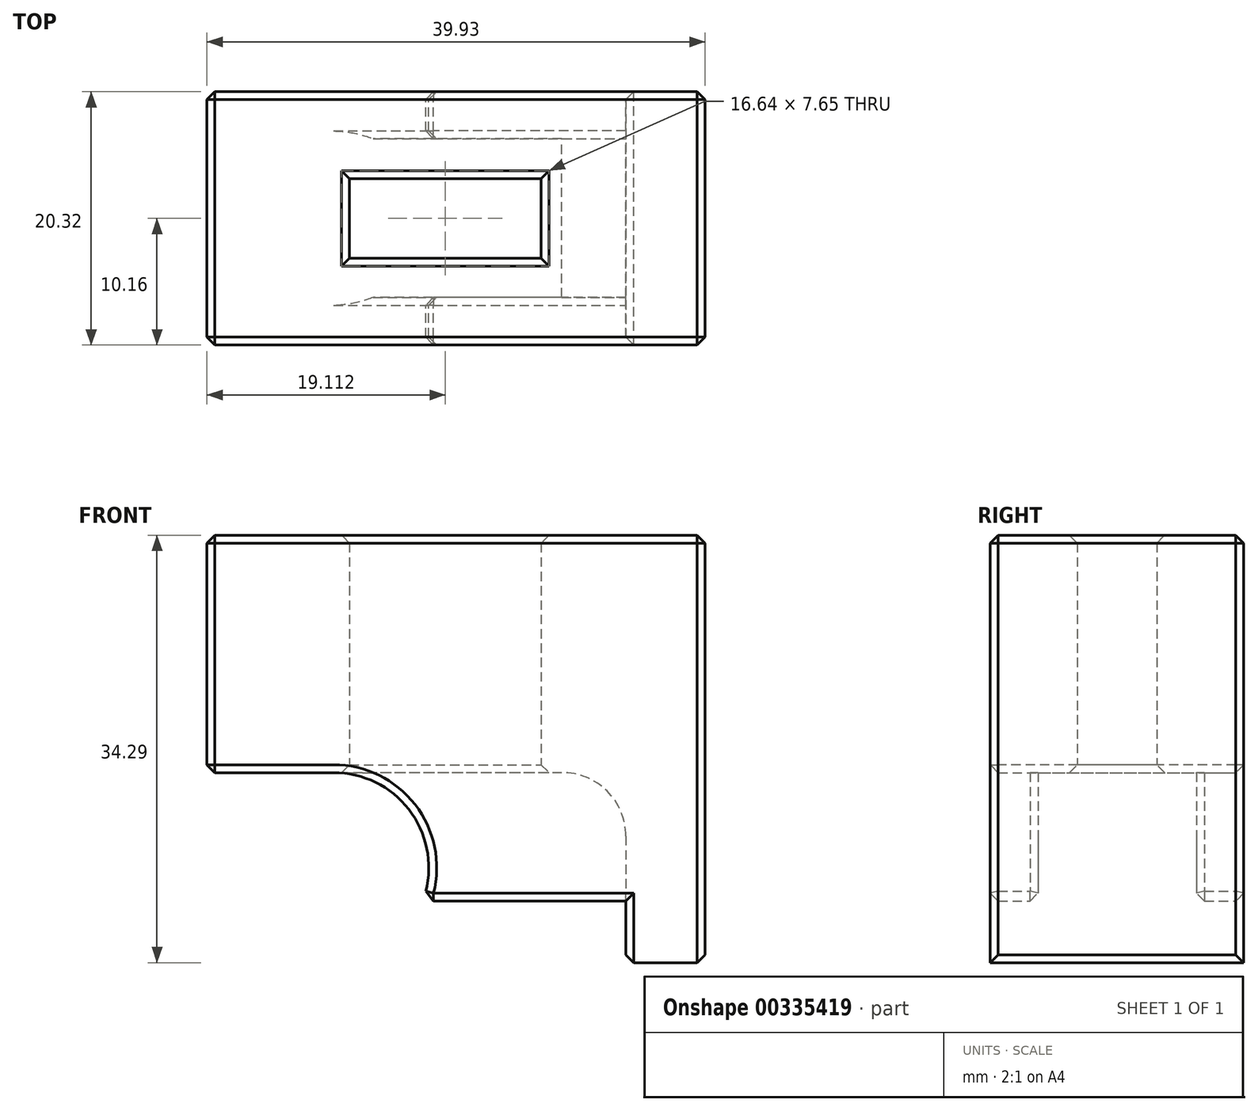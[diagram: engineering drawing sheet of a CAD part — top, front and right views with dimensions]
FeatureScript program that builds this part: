
annotation { "Feature Type Name" : "Feature", "Feature Type Description" : "" }
export const myFeature = defineFeature(function(context is Context, id is Id, definition is map)
    precondition{}
    {
        {
            var Q0;
            Q0=qCreatedBy(makeId("Top.planeOp"),FACE);
            var sketch = newSketch(context, id + "F0", { "sketchPlane" : qUnion([Q0])});
            skLineSegment(sketch, "E0.bottom", {"start": v(4, 3.19) * mm, "end": v(-11.37, 3.19) * mm});
            skLineSegment(sketch, "E0.top", {"start": v(4, -3.19) * mm, "end": v(-11.37, -3.19) * mm});
            skLineSegment(sketch, "E0.left", {"start": v(4, 3.19) * mm, "end": v(4, -3.19) * mm});
            skLineSegment(sketch, "E0.right", {"start": v(-11.37, 3.19) * mm, "end": v(-11.37, -3.19) * mm});
            skPoint(sketch, "E0.middle", {"position": v(-3.69, 0) * mm});
            skLineSegment(sketch, "E1.bottom", {"start": v(10.78, -12.7) * mm, "end": v(-12.64, -12.7) * mm});
            skLineSegment(sketch, "E1.top", {"start": v(10.78, 12.7) * mm, "end": v(-12.64, 12.7) * mm});
            skLineSegment(sketch, "E1.left", {"start": v(10.78, -12.7) * mm, "end": v(10.78, 12.7) * mm});
            skLineSegment(sketch, "E1.right", {"start": v(-12.64, -12.7) * mm, "end": v(-12.64, 12.7) * mm});
            skPoint(sketch, "E1.middle", {"position": v(-0.93, 0) * mm});
            skSolve(sketch);
        }
        {
            var Q0;
            Q0 = qSketchRegion(id + "F0", true);
            extrude(context, id + "F1", {"entities" : qUnion([Q0]), "depth" : 34.3 * mm});
        }
        {
            var Q0;
            Q0=makeQuery(id+"F1.opExtrude","SWEPT_FACE",FACE,{"disambiguationData":[OSD([sQuery(id+"F0.wireOp",EDGE,"E1.top")])]});
            var sketch = newSketch(context, id + "F2", { "sketchPlane" : qUnion([Q0])});
            skCircle(sketch, "E2", {"center": v(12.64, 7.62) * mm, "radius": 7.62 * mm});
            skSolve(sketch);
        }
        {
            var Q0;
            Q0 = qSketchRegion(id + "F2", true);
            extrude(context, id + "F3", {"entities" : qUnion([Q0]), "operationType" : NewBodyOperationType.REMOVE, "oppositeDirection" : true, "depth" : 25.4 * mm});
        }
        {
            var Q0;
            Q0=makeQuery(id+"F1.opExtrude","SWEPT_FACE",FACE,{"disambiguationData":[OSD([sQuery(id+"F0.wireOp",EDGE,"E1.right")])]});
            var sketch = newSketch(context, id + "F4", { "sketchPlane" : qUnion([Q0])});
            skLineSegment(sketch, "E3.bottom", {"start": v(-6.38, 15.24) * mm, "end": v(6.34, 15.24) * mm});
            skLineSegment(sketch, "E3.top", {"start": v(-6.38, 0) * mm, "end": v(6.34, 0) * mm});
            skLineSegment(sketch, "E3.left", {"start": v(-6.38, 15.24) * mm, "end": v(-6.38, 0) * mm});
            skLineSegment(sketch, "E3.right", {"start": v(6.34, 15.24) * mm, "end": v(6.34, 0) * mm});
            skSolve(sketch);
        }
        {
            var Q0;
            Q0 = qSketchRegion(id + "F4", true);
            extrude(context, id + "F5", {"entities" : qUnion([Q0]), "operationType" : NewBodyOperationType.REMOVE, "oppositeDirection" : true, "depth" : 18.29 * mm});
        }
        {
            var Q0;
            Q0=makeQuery(id+"F1.opExtrude","SWEPT_FACE",FACE,{"disambiguationData":[OSD([sQuery(id+"F0.wireOp",EDGE,"E1.left")])]});
            var sketch = newSketch(context, id + "F6", { "sketchPlane" : qUnion([Q0])});
            skLineSegment(sketch, "E4.bottom", {"start": v(-12.7, 34.3) * mm, "end": v(12.7, 34.3) * mm});
            skLineSegment(sketch, "E4.top", {"start": v(-12.7, 0) * mm, "end": v(12.7, 0) * mm});
            skLineSegment(sketch, "E4.left", {"start": v(-12.7, 34.3) * mm, "end": v(-12.7, 0) * mm});
            skLineSegment(sketch, "E4.right", {"start": v(12.7, 34.3) * mm, "end": v(12.7, 0) * mm});
            skSolve(sketch);
        }
        {
            var Q0;
            Q0 = qSketchRegion(id + "F6", true);
            extrude(context, id + "F7", {"entities" : qUnion([Q0]), "operationType" : NewBodyOperationType.ADD, "depth" : 6.35 * mm});
        }
        {
            var Q0;
            Q0=makeQuery(id+"F7.boolean.opBoolean","MERGE",FACE,{"derivedFrom":[makeQuery(id+"F1.opExtrude","SWEPT_FACE",FACE,{"disambiguationData":[OSD([sQuery(id+"F0.wireOp",EDGE,"E1.top")])]}),makeQuery(id+"F7.opExtrude","SWEPT_FACE",FACE,{"disambiguationData":[OSD([sQuery(id+"F6.wireOp",EDGE,"E4.right")])]})]});
            cPlane(context, id + "F8", {"entities" : qUnion([Q0]), "cplaneType" : CPlaneType.OFFSET, "offset" : 6.32 * mm, "oppositeDirection" : true, "width" : 152.4 * mm, "height" : 152.4 * mm});
        }
        {
            var Q0;
            Q0=qCreatedBy(id+"F8.planeOp",FACE);
            var sketch = newSketch(context, id + "F9", { "sketchPlane" : qUnion([Q0])});
            skCircle(sketch, "E5", {"center": v(-5.7, 10.16) * mm, "radius": 5.08 * mm});
            skLineSegment(sketch, "E6", {"start": v(-10.78, 10.16) * mm, "end": v(-10.78, 0) * mm});
            skLineSegment(sketch, "E7", {"start": v(-10.78, 0) * mm, "end": v(-0.62, 0) * mm});
            skLineSegment(sketch, "E8", {"start": v(-0.62, 0) * mm, "end": v(-0.62, 10.16) * mm});
            skSolve(sketch);
        }
        {
            var Q0;
            Q0 = qSketchRegion(id + "F9", true);
            extrude(context, id + "F10", {"entities" : qUnion([Q0]), "operationType" : NewBodyOperationType.REMOVE, "oppositeDirection" : true, "depth" : 12.71 * mm});
        }
        {
            var Q0;
            Q0=makeQuery(id+"F7.boolean.opBoolean","MERGE",FACE,{"derivedFrom":[makeQuery(id+"F1.opExtrude","SWEPT_FACE",FACE,{"disambiguationData":[OSD([sQuery(id+"F0.wireOp",EDGE,"E1.top")])]}),makeQuery(id+"F7.opExtrude","SWEPT_FACE",FACE,{"disambiguationData":[OSD([sQuery(id+"F6.wireOp",EDGE,"E4.right")])]})]});
            var sketch = newSketch(context, id + "F11", { "sketchPlane" : qUnion([Q0])});
            skLineSegment(sketch, "E9.bottom", {"start": v(12.64, 4.93) * mm, "end": v(-10.78, 4.93) * mm});
            skLineSegment(sketch, "E9.top", {"start": v(12.64, -3.43) * mm, "end": v(-10.78, -3.43) * mm});
            skLineSegment(sketch, "E9.left", {"start": v(12.64, 4.93) * mm, "end": v(12.64, -3.43) * mm});
            skLineSegment(sketch, "E9.right", {"start": v(-10.78, 4.93) * mm, "end": v(-10.78, -3.43) * mm});
            skSolve(sketch);
        }
        {
            var Q0;
            Q0 = qSketchRegion(id + "F11", true);
            extrude(context, id + "F12", {"entities" : qUnion([Q0]), "operationType" : NewBodyOperationType.REMOVE, "oppositeDirection" : true, "depth" : 25.4 * mm});
        }
        {
            var Q0;
            Q0=makeQuery(id+"F1.opExtrude","SWEPT_FACE",FACE,{"disambiguationData":[OSD([sQuery(id+"F0.wireOp",EDGE,"E1.right")])]});
            var sketch = newSketch(context, id + "F13", { "sketchPlane" : qUnion([Q0])});
            skLineSegment(sketch, "E10.bottom", {"start": v(-12.7, 34.3) * mm, "end": v(-10.16, 34.3) * mm});
            skLineSegment(sketch, "E10.top", {"start": v(-12.7, 0) * mm, "end": v(-10.16, 0) * mm});
            skLineSegment(sketch, "E10.left", {"start": v(-12.7, 34.3) * mm, "end": v(-12.7, 0) * mm});
            skLineSegment(sketch, "E10.right", {"start": v(-10.16, 34.3) * mm, "end": v(-10.16, 0) * mm});
            skLineSegment(sketch, "E11.bottom", {"start": v(12.7, 34.3) * mm, "end": v(10.16, 34.3) * mm});
            skLineSegment(sketch, "E11.top", {"start": v(12.7, 0) * mm, "end": v(10.16, 0) * mm});
            skLineSegment(sketch, "E11.left", {"start": v(12.7, 34.3) * mm, "end": v(12.7, 0) * mm});
            skLineSegment(sketch, "E11.right", {"start": v(10.16, 34.3) * mm, "end": v(10.16, 0) * mm});
            skSolve(sketch);
        }
        {
            var Q0;
            Q0 = qSketchRegion(id + "F13", true);
            extrude(context, id + "F14", {"entities" : qUnion([Q0]), "operationType" : NewBodyOperationType.REMOVE, "endBound" : BoundingType.THROUGH_ALL, "oppositeDirection" : true, "depth" : 25.4 * mm});
        }
        {
            var Q0;
            Q0=makeQuery(id+"F1.opExtrude","SWEPT_FACE",FACE,{"disambiguationData":[OSD([sQuery(id+"F0.wireOp",EDGE,"E1.right")])]});
            var sketch = newSketch(context, id + "F15", { "sketchPlane" : qUnion([Q0])});
            skLineSegment(sketch, "E12.bottom", {"start": v(-10.16, 15.24) * mm, "end": v(10.16, 15.24) * mm});
            skLineSegment(sketch, "E12.top", {"start": v(-10.16, 34.3) * mm, "end": v(10.16, 34.3) * mm});
            skLineSegment(sketch, "E12.left", {"start": v(-10.16, 15.24) * mm, "end": v(-10.16, 34.3) * mm});
            skLineSegment(sketch, "E12.right", {"start": v(10.16, 15.24) * mm, "end": v(10.16, 34.3) * mm});
            skSolve(sketch);
        }
        {
            var Q0;
            Q0 = qSketchRegion(id + "F15", true);
            extrude(context, id + "F16", {"entities" : qUnion([Q0]), "operationType" : NewBodyOperationType.ADD, "depth" : 10.16 * mm});
        }
        {
            var Q0;
            Q0=makeQuery(id+"F1.opExtrude","CAP_EDGE",EDGE,{"disambiguationData":[OSD([sQuery(id+"F0.wireOp",EDGE,"E0.top")])],"isStart":false});
            var Q1;
            Q1=makeQuery(id+"F1.opExtrude","CAP_EDGE",EDGE,{"disambiguationData":[OSD([sQuery(id+"F0.wireOp",EDGE,"E0.left")])],"isStart":false});
            var Q2;
            Q2=makeQuery(id+"F1.opExtrude","CAP_EDGE",EDGE,{"disambiguationData":[OSD([sQuery(id+"F0.wireOp",EDGE,"E0.bottom")])],"isStart":false});
            var Q3;
            Q3=makeQuery(id+"F1.opExtrude","CAP_EDGE",EDGE,{"disambiguationData":[OSD([sQuery(id+"F0.wireOp",EDGE,"E0.right")])],"isStart":false});
            var Q4;
            Q4=makeQuery(id+"F16.boolean.opBoolean","MERGE",EDGE,{"derivedFrom":[makeQuery(id+"F14.boolean.opBoolean","COPY",EDGE,{"derivedFrom":makeQuery(id+"F14.opExtrude","SWEPT_EDGE",EDGE,{"disambiguationData":[OSD([sQuery(id+"F0.wireOp",EDGE,"E1.right"),sQuery(id+"F13.wireOp",EDGE,"E10.bottom"),sQuery(id+"F13.wireOp",EDGE,"E10.right")])]})}),makeQuery(id+"F16.opExtrude","SWEPT_EDGE",EDGE,{"disambiguationData":[OSD([sQuery(id+"F15.wireOp",EDGE,"E12.top"),sQuery(id+"F15.wireOp",EDGE,"E12.left")])]})]});
            var Q5;
            Q5=makeQuery(id+"F7.opExtrude","CAP_EDGE",EDGE,{"disambiguationData":[OSD([sQuery(id+"F6.wireOp",EDGE,"E4.bottom")])],"isStart":false});
            var Q6;
            Q6=makeQuery(id+"F16.boolean.opBoolean","MERGE",FACE,{"derivedFrom":[makeQuery(id+"F7.boolean.opBoolean","MERGE",FACE,{"derivedFrom":[makeQuery(id+"F1.opExtrude","CAP_FACE",FACE,{"disambiguationData":[OSD([sQuery(id+"F0.wireOp",EDGE,"E0.bottom"),sQuery(id+"F0.wireOp",EDGE,"E0.top"),sQuery(id+"F0.wireOp",EDGE,"E0.left"),sQuery(id+"F0.wireOp",EDGE,"E0.right"),sQuery(id+"F0.wireOp",EDGE,"E1.bottom"),sQuery(id+"F0.wireOp",EDGE,"E1.top"),sQuery(id+"F0.wireOp",EDGE,"E1.left"),sQuery(id+"F0.wireOp",EDGE,"E1.right")])],"isStart":false}),makeQuery(id+"F7.opExtrude","SWEPT_FACE",FACE,{"disambiguationData":[OSD([sQuery(id+"F6.wireOp",EDGE,"E4.bottom")])]})]}),makeQuery(id+"F16.opExtrude","SWEPT_FACE",FACE,{"disambiguationData":[OSD([sQuery(id+"F15.wireOp",EDGE,"E12.top")])]})]});
            var Q7;
            Q7=makeQuery(id+"F16.opExtrude","CAP_EDGE",EDGE,{"disambiguationData":[OSD([sQuery(id+"F15.wireOp",EDGE,"E12.left")])],"isStart":false});
            var Q8;
            Q8=makeQuery(id+"F14.boolean.opBoolean","INTERSECT",EDGE,{"derivedFrom":[makeQuery(id+"F12.boolean.opBoolean","COPY",FACE,{"disambiguationData":[TD([makeQuery(id+"F1.opExtrude","SWEPT_FACE",FACE,{"disambiguationData":[OSD([sQuery(id+"F0.wireOp",EDGE,"E1.top")])]})])],"derivedFrom":makeQuery(id+"F12.opExtrude","SWEPT_FACE",FACE,{"disambiguationData":[OSD([sQuery(id+"F11.wireOp",EDGE,"E9.bottom")])]})}),makeQuery(id+"F14.opExtrude","SWEPT_FACE",FACE,{"disambiguationData":[OSD([sQuery(id+"F13.wireOp",EDGE,"E10.right")])]})]});
            var Q9;
            Q9=makeQuery(id+"F14.boolean.opBoolean","INTERSECT",EDGE,{"derivedFrom":[makeQuery(id+"F12.boolean.opBoolean","MERGE",FACE,{"derivedFrom":[makeQuery(id+"F10.boolean.opBoolean","COPY",FACE,{"derivedFrom":makeQuery(id+"F10.opExtrude","SWEPT_FACE",FACE,{"disambiguationData":[OSD([sQuery(id+"F9.wireOp",EDGE,"E6")])]})}),makeQuery(id+"F12.opExtrude","SWEPT_FACE",FACE,{"disambiguationData":[OSD([sQuery(id+"F11.wireOp",EDGE,"E9.right")])]})]}),makeQuery(id+"F14.opExtrude","SWEPT_FACE",FACE,{"disambiguationData":[OSD([sQuery(id+"F13.wireOp",EDGE,"E10.right")])]})]});
            var Q10;
            Q10=makeQuery(id+"F14.boolean.opBoolean","INTERSECT",EDGE,{"derivedFrom":[makeQuery(id+"F7.opExtrude","CAP_FACE",FACE,{"disambiguationData":[OSD([sQuery(id+"F6.wireOp",EDGE,"E4.bottom"),sQuery(id+"F6.wireOp",EDGE,"E4.top"),sQuery(id+"F6.wireOp",EDGE,"E4.left"),sQuery(id+"F6.wireOp",EDGE,"E4.right")])],"isStart":false}),makeQuery(id+"F14.opExtrude","SWEPT_FACE",FACE,{"disambiguationData":[OSD([sQuery(id+"F13.wireOp",EDGE,"E10.right")])]})]});
            var Q11;
            Q11=makeQuery(id+"F16.opExtrude","CAP_EDGE",EDGE,{"disambiguationData":[OSD([sQuery(id+"F15.wireOp",EDGE,"E12.right")])],"isStart":false});
            var Q12;
            Q12=makeQuery(id+"F16.opExtrude","CAP_EDGE",EDGE,{"disambiguationData":[OSD([sQuery(id+"F15.wireOp",EDGE,"E12.bottom")])],"isStart":false});
            var Q13;
            Q13=makeQuery(id+"F16.opExtrude","SWEPT_EDGE",EDGE,{"disambiguationData":[OSD([sQuery(id+"F15.wireOp",EDGE,"E12.bottom"),sQuery(id+"F15.wireOp",EDGE,"E12.right")])]});
            var Q14;
            Q14=makeQuery(id+"F16.opExtrude","SWEPT_EDGE",EDGE,{"disambiguationData":[OSD([sQuery(id+"F15.wireOp",EDGE,"E12.bottom"),sQuery(id+"F15.wireOp",EDGE,"E12.left")])]});
            var Q15;
            Q15=makeQuery(id+"F12.boolean.opBoolean","INTERSECT",EDGE,{"derivedFrom":[makeQuery(id+"F10.boolean.opBoolean","MERGE",FACE,{"derivedFrom":[makeQuery(id+"F5.boolean.opBoolean","COPY",FACE,{"derivedFrom":makeQuery(id+"F5.opExtrude","SWEPT_FACE",FACE,{"disambiguationData":[OSD([sQuery(id+"F4.wireOp",EDGE,"E3.left")])]})}),makeQuery(id+"F10.opExtrude","CAP_FACE",FACE,{"disambiguationData":[OSD([sQuery(id+"F9.wireOp",EDGE,"E5"),sQuery(id+"F9.wireOp",EDGE,"E6"),sQuery(id+"F9.wireOp",EDGE,"E7"),sQuery(id+"F9.wireOp",EDGE,"E8")])],"isStart":true})]}),makeQuery(id+"F12.opExtrude","SWEPT_FACE",FACE,{"disambiguationData":[OSD([sQuery(id+"F11.wireOp",EDGE,"E9.bottom")])]})]});
            var Q16;
            {var subQ1=sQuery(id+"F0.wireOp",EDGE,"E1.top");Q16=makeQuery(id+"F12.boolean.opBoolean","INTERSECT",EDGE,{"derivedFrom":[makeQuery(id+"F5.boolean.opBoolean","SPLIT",FACE,{"disambiguationData":[TD([makeQuery(id+"F1.opExtrude","SWEPT_FACE",FACE,{"disambiguationData":[OSD([subQ1])]})])],"derivedFrom":makeQuery(id+"F3.boolean.opBoolean","COPY",FACE,{"derivedFrom":makeQuery(id+"F3.opExtrude","SWEPT_FACE",FACE,{"disambiguationData":[OSD([sQuery(id+"F2.wireOp",EDGE,"E2")])]})})}),makeQuery(id+"F12.opExtrude","SWEPT_FACE",FACE,{"disambiguationData":[OSD([sQuery(id+"F11.wireOp",EDGE,"E9.bottom")])]})]});}
            var Q17;
            Q17=makeQuery(id+"F5.boolean.opBoolean","INTERSECT",EDGE,{"derivedFrom":[makeQuery(id+"F3.boolean.opBoolean","COPY",FACE,{"derivedFrom":makeQuery(id+"F3.opExtrude","SWEPT_FACE",FACE,{"disambiguationData":[OSD([sQuery(id+"F2.wireOp",EDGE,"E2")])]})}),makeQuery(id+"F5.opExtrude","SWEPT_FACE",FACE,{"disambiguationData":[OSD([sQuery(id+"F4.wireOp",EDGE,"E3.left")])]})]});
            var Q18;
            Q18=makeQuery(id+"F5.boolean.opBoolean","INTERSECT",EDGE,{"derivedFrom":[makeQuery(id+"F3.boolean.opBoolean","COPY",FACE,{"derivedFrom":makeQuery(id+"F3.opExtrude","SWEPT_FACE",FACE,{"disambiguationData":[OSD([sQuery(id+"F2.wireOp",EDGE,"E2")])]})}),makeQuery(id+"F5.opExtrude","SWEPT_FACE",FACE,{"disambiguationData":[OSD([sQuery(id+"F4.wireOp",EDGE,"E3.right")])]})]});
            var Q19;
            {var subQ0=sQuery(id+"F0.wireOp",EDGE,"E1.bottom");Q19=makeQuery(id+"F12.boolean.opBoolean","INTERSECT",EDGE,{"derivedFrom":[makeQuery(id+"F5.boolean.opBoolean","SPLIT",FACE,{"disambiguationData":[TD([makeQuery(id+"F1.opExtrude","SWEPT_FACE",FACE,{"disambiguationData":[OSD([subQ0])]})])],"derivedFrom":makeQuery(id+"F3.boolean.opBoolean","COPY",FACE,{"derivedFrom":makeQuery(id+"F3.opExtrude","SWEPT_FACE",FACE,{"disambiguationData":[OSD([sQuery(id+"F2.wireOp",EDGE,"E2")])]})})}),makeQuery(id+"F12.opExtrude","SWEPT_FACE",FACE,{"disambiguationData":[OSD([sQuery(id+"F11.wireOp",EDGE,"E9.bottom")])]})]});}
            var Q20;
            Q20=makeQuery(id+"F12.boolean.opBoolean","INTERSECT",EDGE,{"derivedFrom":[makeQuery(id+"F10.boolean.opBoolean","MERGE",FACE,{"derivedFrom":[makeQuery(id+"F5.boolean.opBoolean","COPY",FACE,{"derivedFrom":makeQuery(id+"F5.opExtrude","SWEPT_FACE",FACE,{"disambiguationData":[OSD([sQuery(id+"F4.wireOp",EDGE,"E3.right")])]})}),makeQuery(id+"F10.opExtrude","CAP_FACE",FACE,{"disambiguationData":[OSD([sQuery(id+"F9.wireOp",EDGE,"E5"),sQuery(id+"F9.wireOp",EDGE,"E6"),sQuery(id+"F9.wireOp",EDGE,"E7"),sQuery(id+"F9.wireOp",EDGE,"E8")])],"isStart":false})]}),makeQuery(id+"F12.opExtrude","SWEPT_FACE",FACE,{"disambiguationData":[OSD([sQuery(id+"F11.wireOp",EDGE,"E9.bottom")])]})]});
            var Q21;
            Q21=makeQuery(id+"F12.boolean.opBoolean","INTERSECT",EDGE,{"derivedFrom":[makeQuery(id+"F7.boolean.opBoolean","MERGE",FACE,{"derivedFrom":[makeQuery(id+"F1.opExtrude","CAP_FACE",FACE,{"disambiguationData":[OSD([sQuery(id+"F0.wireOp",EDGE,"E0.bottom"),sQuery(id+"F0.wireOp",EDGE,"E0.top"),sQuery(id+"F0.wireOp",EDGE,"E0.left"),sQuery(id+"F0.wireOp",EDGE,"E0.right"),sQuery(id+"F0.wireOp",EDGE,"E1.bottom"),sQuery(id+"F0.wireOp",EDGE,"E1.top"),sQuery(id+"F0.wireOp",EDGE,"E1.left"),sQuery(id+"F0.wireOp",EDGE,"E1.right")])],"isStart":true}),makeQuery(id+"F7.opExtrude","SWEPT_FACE",FACE,{"disambiguationData":[OSD([sQuery(id+"F6.wireOp",EDGE,"E4.top")])]})]}),makeQuery(id+"F12.opExtrude","SWEPT_FACE",FACE,{"disambiguationData":[OSD([sQuery(id+"F11.wireOp",EDGE,"E9.right")])]})]});
            var Q22;
            Q22=makeQuery(id+"F14.boolean.opBoolean","COPY",EDGE,{"derivedFrom":makeQuery(id+"F14.opExtrude","SWEPT_EDGE",EDGE,{"disambiguationData":[OSD([sQuery(id+"F13.wireOp",EDGE,"E10.top"),sQuery(id+"F13.wireOp",EDGE,"E10.right")])]})});
            var Q23;
            Q23=makeQuery(id+"F7.opExtrude","CAP_EDGE",EDGE,{"disambiguationData":[OSD([sQuery(id+"F6.wireOp",EDGE,"E4.top")])],"isStart":false});
            var Q24;
            Q24=makeQuery(id+"F14.boolean.opBoolean","INTERSECT",EDGE,{"derivedFrom":[makeQuery(id+"F12.boolean.opBoolean","COPY",FACE,{"disambiguationData":[TD([makeQuery(id+"F1.opExtrude","SWEPT_FACE",FACE,{"disambiguationData":[OSD([sQuery(id+"F0.wireOp",EDGE,"E1.bottom")])]})])],"derivedFrom":makeQuery(id+"F12.opExtrude","SWEPT_FACE",FACE,{"disambiguationData":[OSD([sQuery(id+"F11.wireOp",EDGE,"E9.bottom")])]})}),makeQuery(id+"F14.opExtrude","SWEPT_FACE",FACE,{"disambiguationData":[OSD([sQuery(id+"F13.wireOp",EDGE,"E11.right")])]})]});
            var Q25;
            Q25=makeQuery(id+"F14.boolean.opBoolean","INTERSECT",EDGE,{"derivedFrom":[makeQuery(id+"F12.boolean.opBoolean","MERGE",FACE,{"derivedFrom":[makeQuery(id+"F10.boolean.opBoolean","COPY",FACE,{"derivedFrom":makeQuery(id+"F10.opExtrude","SWEPT_FACE",FACE,{"disambiguationData":[OSD([sQuery(id+"F9.wireOp",EDGE,"E6")])]})}),makeQuery(id+"F12.opExtrude","SWEPT_FACE",FACE,{"disambiguationData":[OSD([sQuery(id+"F11.wireOp",EDGE,"E9.right")])]})]}),makeQuery(id+"F14.opExtrude","SWEPT_FACE",FACE,{"disambiguationData":[OSD([sQuery(id+"F13.wireOp",EDGE,"E11.right")])]})]});
            var Q26;
            Q26=makeQuery(id+"F14.boolean.opBoolean","COPY",EDGE,{"derivedFrom":makeQuery(id+"F14.opExtrude","SWEPT_EDGE",EDGE,{"disambiguationData":[OSD([sQuery(id+"F13.wireOp",EDGE,"E11.top"),sQuery(id+"F13.wireOp",EDGE,"E11.right")])]})});
            var Q27;
            Q27=makeQuery(id+"F14.boolean.opBoolean","INTERSECT",EDGE,{"derivedFrom":[makeQuery(id+"F7.opExtrude","CAP_FACE",FACE,{"disambiguationData":[OSD([sQuery(id+"F6.wireOp",EDGE,"E4.bottom"),sQuery(id+"F6.wireOp",EDGE,"E4.top"),sQuery(id+"F6.wireOp",EDGE,"E4.left"),sQuery(id+"F6.wireOp",EDGE,"E4.right")])],"isStart":false}),makeQuery(id+"F14.opExtrude","SWEPT_FACE",FACE,{"disambiguationData":[OSD([sQuery(id+"F13.wireOp",EDGE,"E11.right")])]})]});
            var Q28;
            Q28=makeQuery(id+"F5.boolean.opBoolean","INTERSECT",EDGE,{"derivedFrom":[makeQuery(id+"F1.opExtrude","SWEPT_FACE",FACE,{"disambiguationData":[OSD([sQuery(id+"F0.wireOp",EDGE,"E0.bottom")])]}),makeQuery(id+"F5.opExtrude","SWEPT_FACE",FACE,{"disambiguationData":[OSD([sQuery(id+"F4.wireOp",EDGE,"E3.bottom")])]})]});
            var Q29;
            Q29=makeQuery(id+"F5.boolean.opBoolean","INTERSECT",EDGE,{"derivedFrom":[makeQuery(id+"F1.opExtrude","SWEPT_FACE",FACE,{"disambiguationData":[OSD([sQuery(id+"F0.wireOp",EDGE,"E0.left")])]}),makeQuery(id+"F5.opExtrude","SWEPT_FACE",FACE,{"disambiguationData":[OSD([sQuery(id+"F4.wireOp",EDGE,"E3.bottom")])]})]});
            var Q30;
            Q30=makeQuery(id+"F5.boolean.opBoolean","INTERSECT",EDGE,{"derivedFrom":[makeQuery(id+"F1.opExtrude","SWEPT_FACE",FACE,{"disambiguationData":[OSD([sQuery(id+"F0.wireOp",EDGE,"E0.top")])]}),makeQuery(id+"F5.opExtrude","SWEPT_FACE",FACE,{"disambiguationData":[OSD([sQuery(id+"F4.wireOp",EDGE,"E3.bottom")])]})]});
            var Q31;
            {var subQ0=sQuery(id+"F0.wireOp",EDGE,"E0.bottom");var subQ1=sQuery(id+"F0.wireOp",EDGE,"E0.right");var subQ2=sQuery(id+"F0.wireOp",EDGE,"E0.top");Q31=makeQuery(id+"F5.boolean.opBoolean","INTERSECT",EDGE,{"derivedFrom":[makeQuery(id+"F3.boolean.opBoolean","SPLIT",FACE,{"disambiguationData":[TD([makeQuery(id+"F1.opExtrude","CAP_FACE",FACE,{"disambiguationData":[OSD([subQ0,subQ2,sQuery(id+"F0.wireOp",EDGE,"E0.left"),subQ1,sQuery(id+"F0.wireOp",EDGE,"E1.bottom"),sQuery(id+"F0.wireOp",EDGE,"E1.top"),sQuery(id+"F0.wireOp",EDGE,"E1.left"),sQuery(id+"F0.wireOp",EDGE,"E1.right")])],"isStart":false})])],"derivedFrom":makeQuery(id+"F1.opExtrude","SWEPT_FACE",FACE,{"disambiguationData":[OSD([subQ1])]})}),makeQuery(id+"F5.opExtrude","SWEPT_FACE",FACE,{"disambiguationData":[OSD([sQuery(id+"F4.wireOp",EDGE,"E3.bottom")])]})]});}
            chamfer(context, id + "F17", {"entities" : qUnion([Q0, Q1, Q2, Q3, Q4, Q5, Q6, Q7, Q8, Q9, Q10, Q11, Q12, Q13, Q14, Q15, Q16, Q17, Q18, Q19, Q20, Q21, Q22, Q23, Q24, Q25, Q26, Q27, Q28, Q29, Q30, Q31]), "width" : 0.64 * mm, "tangentPropagation" : true});
        }
    });
